# Revit family: 940-0008_0014
name_source: partatom
category: Mechanical Equipment
revit_build: Autodesk Revit 2013 (Build: 20120221_2030(x64)
units: mm (PartAtom-declared; Revit-internal decimal feet)

## types (2) — shared parameters
Alarm Panel = Nema 4X Polycarbonate
Alarm Panel Cd Length = 120"
Alarm Panel Dimensions = 6" X 6" X 4"
Assembly Code = D2010900
Default Elevation = 0"
Description = Oil Guard Pump Switch and Panel
High Liquid Alarm Switch = High Impact Plastic
High Liquid Alarm Switch Cd Length = 240"
High Liquid Alarm Switch Dimensions = 1.5" w X 3.5" h X 1.5" d
Installation Type = Floor Mounted
Manufacturer = Zoeller
Masterformat Number = 33 36 16
Masterformat Title = Utility Septic Tank Effluent Pumps
Max Flow @ 5' Hd = 100 GPM
Maximum Head = 672"
Omniclass Table 23 Code = 23.60.30.21
Omniclass Table 23 Title = Pumps
Phase = 1
Price = Prices may vary. Please consult Manufacturer Representative for most up-to-date price list.
Product Page URL = http://www.zoellerpumps.com
Pump = Cast Iron-Zoeller-Powder Coated Epoxy
Pump Amps = 15
Pump Discharge Diameter = 1 1/2"
Pump Family = Pump_Commercial-Effluent-Zoeller-161_Single_Seal_Series : 161
Pump HP = 1/2 HP
Pump Height = 18 9/16"
Pump Length = 12 3/4"
Pump Switch = High Impact Plastic
Pump Switch Cd Length (Piggyback) = 240"
Pump Switch Dimensions = 2.5" w X 6" h X 1.75" d
Pump Switch Family = Oil_Smart_System-Zoeller-Pipe_Assembly : Discharge_Pipe_Assembly_With_Plug
Pump Switch Sensor Probe = 6"
Pump Width = 8"
URL = http://www.zoellerpumps.com
Voltage = 115 V
Waste Connection = Yes

## per-type parameters (varying)
| type | Pump Cord Length | SO Jacketed Cord (Oil Resistant) |
| 940-0008 | 240" | No |
| 940-0014 | 6' or 72" | Yes |

note: column(s) folded — value = type name in every type: Model

## geometry (parser evidence)
native form markers: Blend x12, Sweep x9
no freeform markers — native parametric forms only
